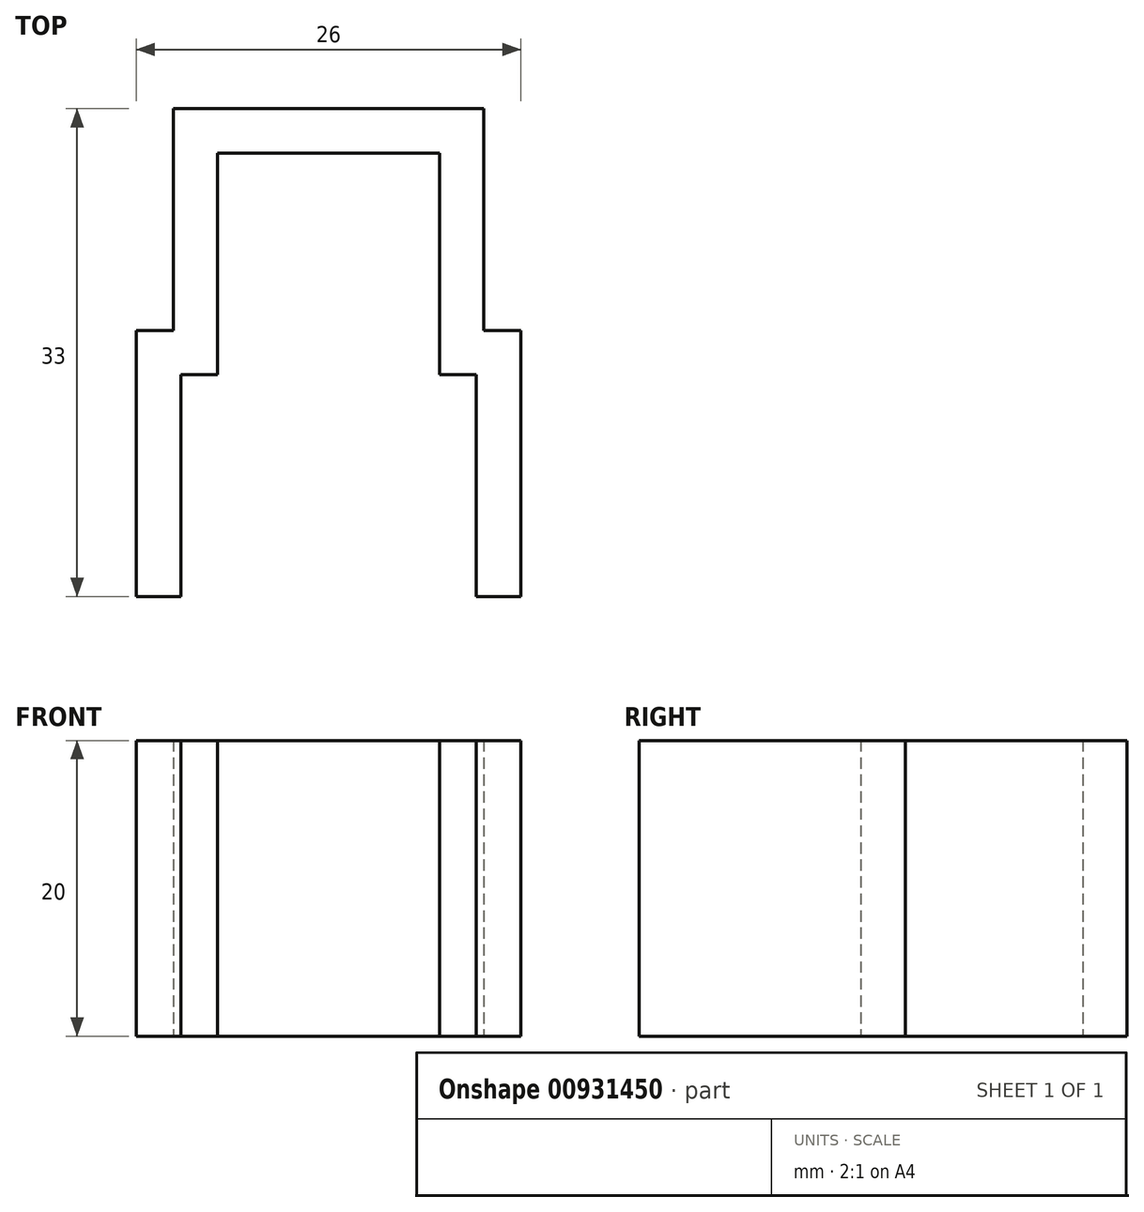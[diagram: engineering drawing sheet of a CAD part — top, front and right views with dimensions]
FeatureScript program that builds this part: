
annotation { "Feature Type Name" : "Feature", "Feature Type Description" : "" }
export const myFeature = defineFeature(function(context is Context, id is Id, definition is map)
    precondition{}
    {
        {
            var Q0;
            Q0=qCreatedBy(makeId("Top.planeOp"),FACE);
            var sketch = newSketch(context, id + "F0", { "sketchPlane" : qUnion([Q0])});
            skLineSegment(sketch, "E0.top", {"start": v(-7.5, 7.5) * mm, "end": v(7.5, 7.5) * mm});
            skLineSegment(sketch, "E0.left", {"start": v(-7.5, -7.5) * mm, "end": v(-7.5, 7.5) * mm});
            skLineSegment(sketch, "E0.right", {"start": v(7.5, -7.5) * mm, "end": v(7.5, 7.5) * mm});
            skPoint(sketch, "E0.middle", {"position": v(0, 0) * mm});
            skLineSegment(sketch, "E1.top", {"start": v(-10, -7.5) * mm, "end": v(-7.5, -7.5) * mm});
            skLineSegment(sketch, "E1.left", {"start": v(-10, -22.5) * mm, "end": v(-10, -7.5) * mm});
            skLineSegment(sketch, "E1.right", {"start": v(10, -22.5) * mm, "end": v(10, -7.5) * mm});
            skPoint(sketch, "E1.middle", {"position": v(0, -15) * mm});
            skPoint(sketch, "E1.middle.positionSnap0", {"position": v(0, -7.5) * mm});
            skPoint(sketch, "E1.centerSnap0", {"position": v(0, -7.5) * mm});
            skLineSegment(sketch, "E2.trimOffspring", {"start": v(7.5, -7.5) * mm, "end": v(10, -7.5) * mm});
            skLineSegment(sketch, "E3.0", {"start": v(13, -22.5) * mm, "end": v(13, -4.5) * mm});
            skLineSegment(sketch, "E3.1", {"start": v(10.5, -4.5) * mm, "end": v(13, -4.5) * mm});
            skLineSegment(sketch, "E3.2", {"start": v(10.5, -4.5) * mm, "end": v(10.5, 10.5) * mm});
            skLineSegment(sketch, "E3.3", {"start": v(-13, -22.5) * mm, "end": v(-13, -4.5) * mm});
            skLineSegment(sketch, "E3.4", {"start": v(-13, -4.5) * mm, "end": v(-10.5, -4.5) * mm});
            skLineSegment(sketch, "E3.5", {"start": v(-10.5, -4.5) * mm, "end": v(-10.5, 10.5) * mm});
            skLineSegment(sketch, "E3.6", {"start": v(-10.5, 10.5) * mm, "end": v(10.5, 10.5) * mm});
            skLineSegment(sketch, "E4", {"start": v(-13, -22.5) * mm, "end": v(-10, -22.5) * mm});
            skLineSegment(sketch, "E5", {"start": v(10, -22.5) * mm, "end": v(13, -22.5) * mm});
            skSolve(sketch);
        }
        {
            var Q0;
            Q0 = qSketchRegion(id + "F0", true);
            extrude(context, id + "F1", {"entities" : qUnion([Q0]), "depth" : 20 * mm, "offsetDistance" : 25 * mm});
        }
    });
